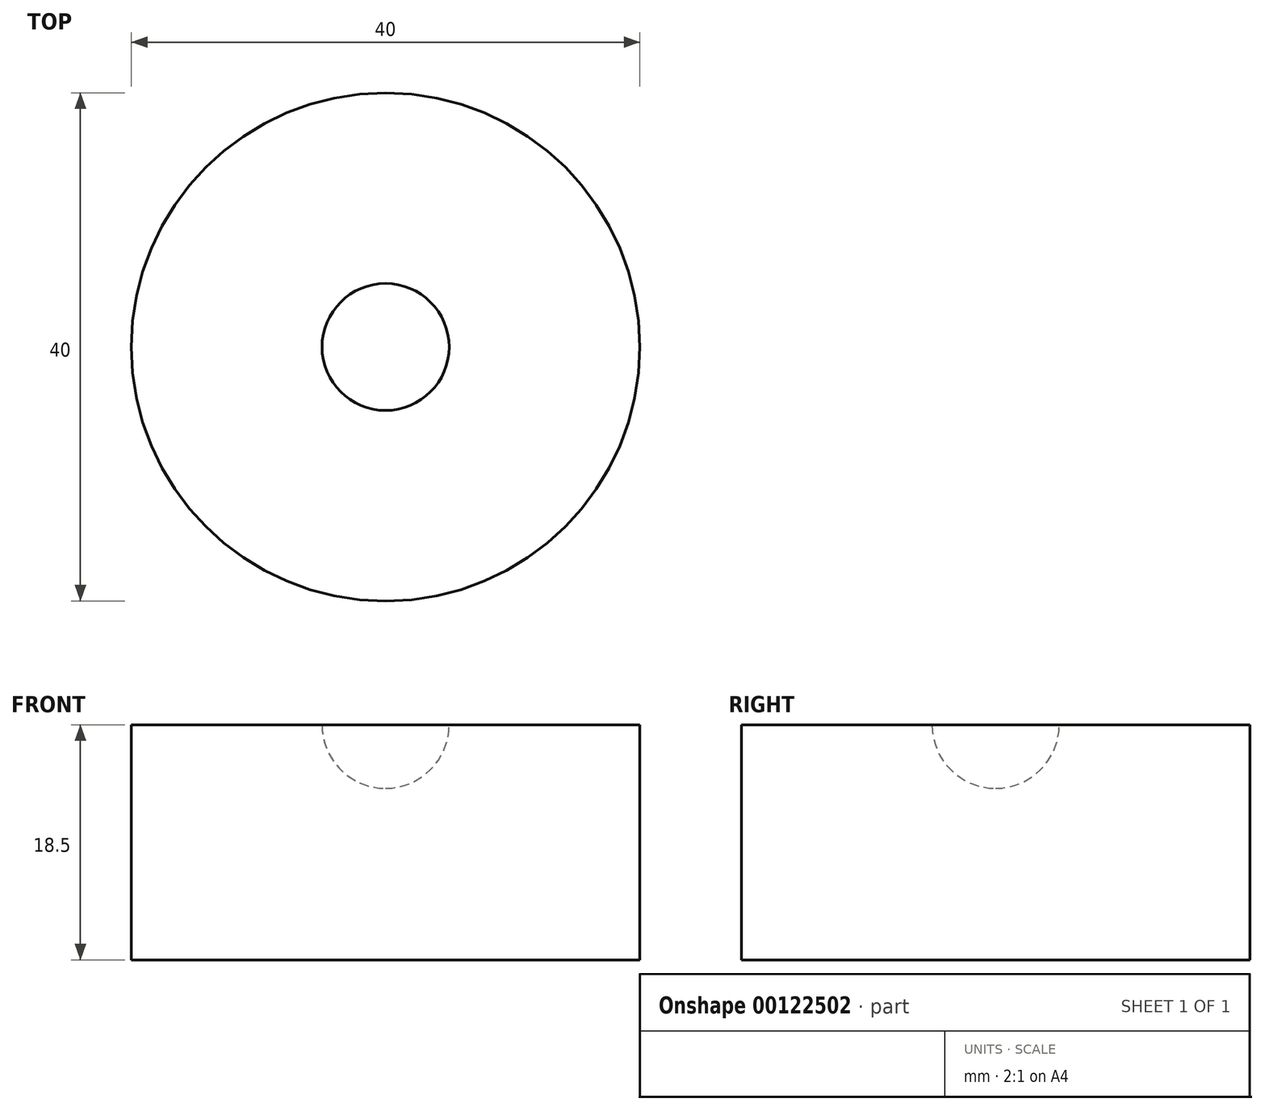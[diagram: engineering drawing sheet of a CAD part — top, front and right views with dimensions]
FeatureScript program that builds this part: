
annotation { "Feature Type Name" : "Feature", "Feature Type Description" : "" }
export const myFeature = defineFeature(function(context is Context, id is Id, definition is map)
    precondition{}
    {
        {
            var Q0;
            Q0=qCreatedBy(makeId("Front.planeOp"),FACE);
            var sketch = newSketch(context, id + "F0", { "sketchPlane" : qUnion([Q0])});
            skLineSegment(sketch, "E0.bottom", {"start": v(0, 0) * mm, "end": v(-20, 0) * mm});
            skLineSegment(sketch, "E0.left", {"start": v(0, 0) * mm, "end": v(0, 13.5) * mm});
            skLineSegment(sketch, "E0.right", {"start": v(-20, 0) * mm, "end": v(-20, 18.5) * mm});
            skLineSegment(sketch, "E1", {"start": v(-5, 18.5) * mm, "end": v(-5, 0) * mm, "construction": true});
            skArc(sketch, "E2", {"start": v(-5, 18.5) * mm, "mid": v(-3.54, 14.96) * mm, "end": v(0, 13.5) * mm});
            skLineSegment(sketch, "E3", {"start": v(-5, 18.5) * mm, "end": v(-20, 18.5) * mm});
            skSolve(sketch);
        }
        {
            var Q0;
            Q0=makeQuery(id+"F0.imprint","IMPRINT",FACE,{"disambiguationData":[TD([[makeQuery(id+"F0.imprint","IMPRINT",EDGE,{"derivedFrom":sQuery(id+"F0.wireOp",EDGE,"E0.bottom")}),-1.0]])]});
            var Q1;
            Q1=sQuery(id+"F0.wireOp",EDGE,"E0.left");
            revolve(context, id + "F1", {"entities" : qUnion([Q0]), "axis" : qUnion([Q1]), "revolveType" : RevolveType.FULL});
        }
    });
